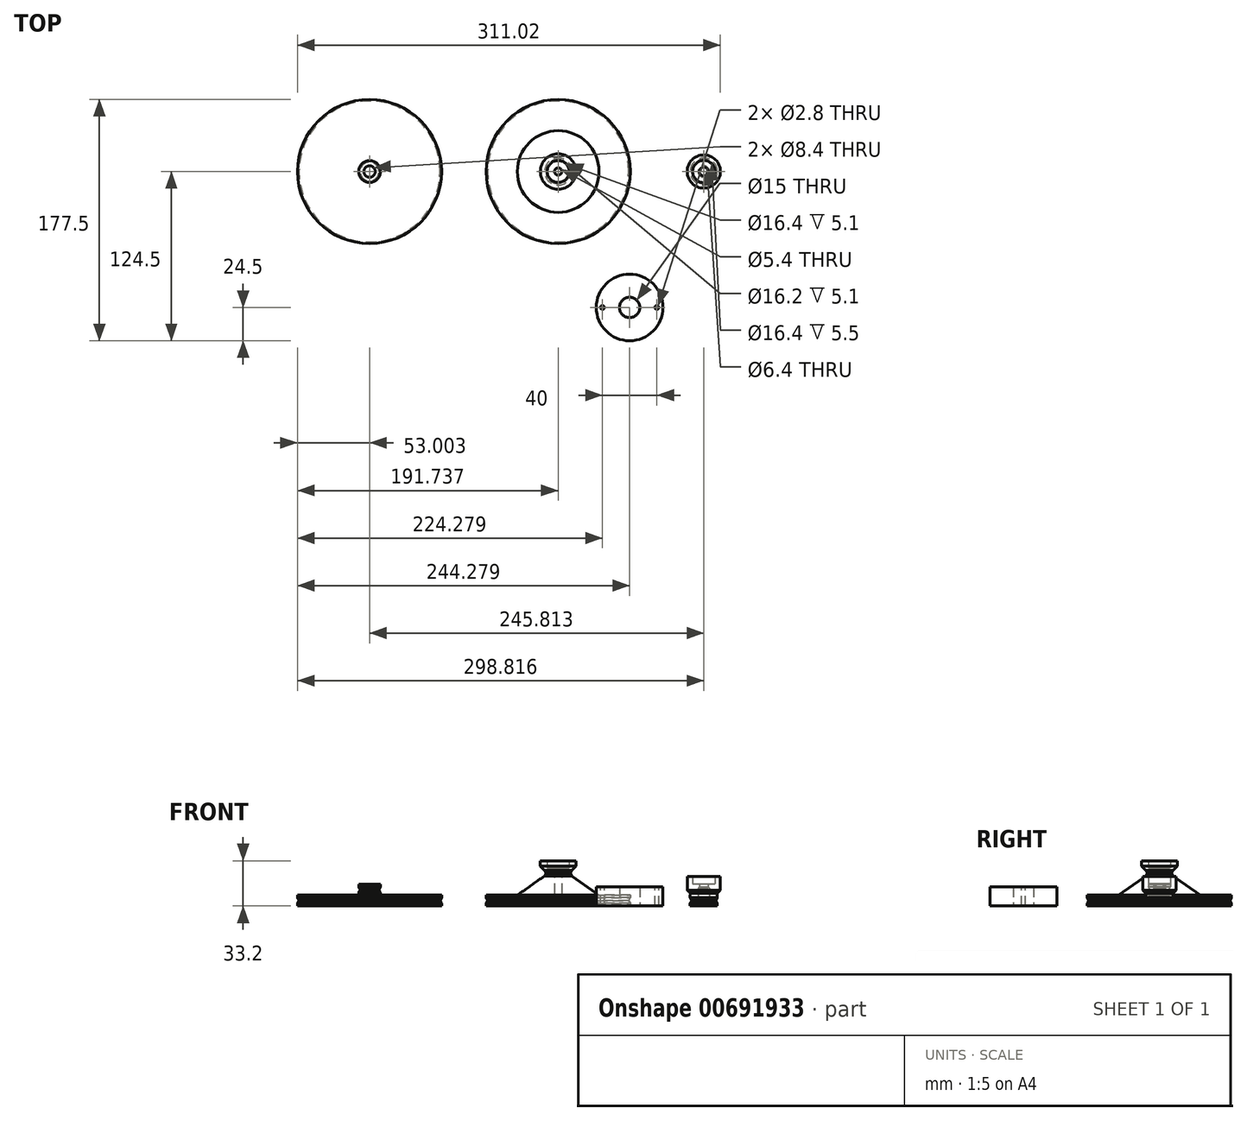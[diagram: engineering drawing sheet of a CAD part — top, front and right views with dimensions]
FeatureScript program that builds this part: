
annotation { "Feature Type Name" : "Feature", "Feature Type Description" : "" }
export const myFeature = defineFeature(function(context is Context, id is Id, definition is map)
    precondition{}
    {
        {
            var Q0;
            Q0=qCreatedBy(makeId("Front.planeOp"),FACE);
            var sketch = newSketch(context, id + "F0", { "sketchPlane" : qUnion([Q0])});
            skLineSegment(sketch, "E0", {"start": v(-130.12, 0) * mm, "end": v(-130.12, 2) * mm});
            skLineSegment(sketch, "E1", {"start": v(-130.12, 8) * mm, "end": v(-87.12, 8) * mm});
            skLineSegment(sketch, "E2", {"start": v(-87.12, 8) * mm, "end": v(-87.12, 22.1) * mm});
            skLineSegment(sketch, "E3", {"start": v(-87.12, 28.1) * mm, "end": v(-79.82, 28.1) * mm});
            skLineSegment(sketch, "E4", {"start": v(-79.82, 28.1) * mm, "end": v(-79.82, 0) * mm});
            skLineSegment(sketch, "E5", {"start": v(-79.82, 0) * mm, "end": v(-130.12, 0) * mm});
            skLineSegment(sketch, "E6", {"start": v(-130.12, 6) * mm, "end": v(-128.97, 4) * mm});
            skLineSegment(sketch, "E7", {"start": v(-128.97, 4) * mm, "end": v(-130.12, 2) * mm});
            skLineSegment(sketch, "E8", {"start": v(-87.12, 26.1) * mm, "end": v(-85.97, 24.1) * mm});
            skLineSegment(sketch, "E9", {"start": v(-85.97, 24.1) * mm, "end": v(-87.12, 22.1) * mm});
            skLineSegment(sketch, "E10.trimOffspring", {"start": v(-87.12, 26.1) * mm, "end": v(-87.12, 28.1) * mm});
            skLineSegment(sketch, "E11.trimOffspring", {"start": v(-130.12, 6) * mm, "end": v(-130.12, 8) * mm});
            skLineSegment(sketch, "E12", {"start": v(-77.12, 0) * mm, "end": v(-77.12, 16.17) * mm, "construction": true});
            skLineSegment(sketch, "E13", {"start": v(25.76, 0) * mm, "end": v(25.76, 16.21) * mm});
            skLineSegment(sketch, "E14", {"start": v(25.76, 16.21) * mm, "end": v(21.76, 16.21) * mm});
            skLineSegment(sketch, "E15", {"start": v(21.76, 16.21) * mm, "end": v(21.76, 21.71) * mm});
            skLineSegment(sketch, "E16", {"start": v(21.76, 21.71) * mm, "end": v(17.76, 21.71) * mm});
            skLineSegment(sketch, "E17", {"start": v(17.76, 21.71) * mm, "end": v(17.76, 11.68) * mm});
            skLineSegment(sketch, "E18", {"start": v(29.96, 0) * mm, "end": v(29.96, 12.69) * mm, "construction": true});
            skLineSegment(sketch, "E19", {"start": v(19.96, 0) * mm, "end": v(19.96, 2) * mm});
            skLineSegment(sketch, "E20", {"start": v(19.96, 2) * mm, "end": v(21.11, 4) * mm});
            skLineSegment(sketch, "E21", {"start": v(21.11, 4) * mm, "end": v(19.96, 6) * mm});
            skLineSegment(sketch, "E22", {"start": v(17.76, 11.68) * mm, "end": v(19.98, 9.41) * mm});
            skLineSegment(sketch, "E23", {"start": v(25.76, 0) * mm, "end": v(19.96, 0) * mm});
            skLineSegment(sketch, "E24", {"start": v(19.98, 9.41) * mm, "end": v(19.96, 6) * mm});
            skLineSegment(sketch, "E25", {"start": v(25.76, 16.21) * mm, "end": v(26.76, 16.21) * mm});
            skLineSegment(sketch, "E26", {"start": v(26.76, 16.21) * mm, "end": v(26.76, 14.02) * mm});
            skLineSegment(sketch, "E27", {"start": v(26.76, 14.02) * mm, "end": v(25.76, 13.02) * mm});
            skLineSegment(sketch, "E28", {"start": v(-268.86, 0) * mm, "end": v(-268.86, 2) * mm});
            skLineSegment(sketch, "E29", {"start": v(-268.86, 8) * mm, "end": v(-223.86, 8) * mm});
            skLineSegment(sketch, "E30", {"start": v(-223.86, 8) * mm, "end": v(-223.86, 10) * mm});
            skLineSegment(sketch, "E31", {"start": v(-223.86, 16) * mm, "end": v(-220.06, 16) * mm});
            skLineSegment(sketch, "E32", {"start": v(-220.06, 16) * mm, "end": v(-220.06, 0) * mm});
            skLineSegment(sketch, "E33", {"start": v(-220.06, 0) * mm, "end": v(-268.86, 0) * mm});
            skLineSegment(sketch, "E34", {"start": v(-268.86, 6) * mm, "end": v(-267.7, 4) * mm});
            skLineSegment(sketch, "E35", {"start": v(-267.7, 4) * mm, "end": v(-268.86, 2) * mm});
            skLineSegment(sketch, "E36", {"start": v(-223.86, 14) * mm, "end": v(-222.7, 12) * mm});
            skLineSegment(sketch, "E37", {"start": v(-222.7, 12) * mm, "end": v(-223.86, 10) * mm});
            skLineSegment(sketch, "E38.trimOffspring", {"start": v(-223.86, 14) * mm, "end": v(-223.86, 16) * mm});
            skLineSegment(sketch, "E39.trimOffspring", {"start": v(-268.86, 6) * mm, "end": v(-268.86, 8) * mm});
            skLineSegment(sketch, "E40", {"start": v(-215.86, 0) * mm, "end": v(-215.86, 22.9) * mm, "construction": true});
            skLineSegment(sketch, "E41", {"start": v(-224.06, 0) * mm, "end": v(-224.06, -5.1) * mm});
            skLineSegment(sketch, "E42", {"start": v(-224.06, -5.1) * mm, "end": v(-234.06, -5.1) * mm});
            skLineSegment(sketch, "E43", {"start": v(-234.06, -5.1) * mm, "end": v(-234.06, 0) * mm});
            skLineSegment(sketch, "E44", {"start": v(-79.82, 5.1) * mm, "end": v(-85.32, 5.1) * mm});
            skLineSegment(sketch, "E45", {"start": v(-85.32, 5.1) * mm, "end": v(-85.32, 0) * mm});
            skLineSegment(sketch, "E46", {"start": v(-87.12, 22.1) * mm, "end": v(-107.16, 8) * mm});
            skLineSegment(sketch, "E47", {"start": v(-85.22, 28.1) * mm, "end": v(-85.22, 33.2) * mm});
            skLineSegment(sketch, "E48", {"start": v(-85.22, 33.2) * mm, "end": v(-90.22, 33.2) * mm});
            skLineSegment(sketch, "E49", {"start": v(-90.22, 33.2) * mm, "end": v(-90.22, 29.2) * mm});
            skLineSegment(sketch, "E50", {"start": v(-90.22, 29.2) * mm, "end": v(-87.12, 26.1) * mm});
            skSolve(sketch);
        }
        {
            var Q0;
            {var subQ0=sQuery(id+"F0.wireOp",EDGE,"E25");Q0=makeQuery(id+"F0.imprint","IMPRINT",FACE,{"disambiguationData":[TD([[makeQuery(id+"F0.imprint","IMPRINT",EDGE,{"derivedFrom":subQ0}),-1.0]])]});}
            var Q1;
            {var subQ3=sQuery(id+"F0.wireOp",EDGE,"E14");Q1=makeQuery(id+"F0.imprint","IMPRINT",FACE,{"disambiguationData":[TD([[makeQuery(id+"F0.imprint","IMPRINT",EDGE,{"derivedFrom":subQ3}),1.0]])]});}
            var Q2;
            Q2=sQuery(id+"F0.wireOp",EDGE,"E18");
            revolve(context, id + "F1", {"surfaceOperationType" : NewSurfaceOperationType.NEW, "entities" : qUnion([Q0, Q1]), "axis" : qUnion([Q2]), "revolveType" : RevolveType.FULL});
        }
        {
            var Q0;
            Q0=makeQuery(id+"F0.imprint","IMPRINT",FACE,{"disambiguationData":[TD([[makeQuery(id+"F0.imprint","IMPRINT",EDGE,{"derivedFrom":sQuery(id+"F0.wireOp",EDGE,"E0")}),-1.0]])]});
            var Q1;
            {var subQ1=sQuery(id+"F0.wireOp",EDGE,"E10.trimOffspring");Q1=makeQuery(id+"F0.imprint","IMPRINT",FACE,{"disambiguationData":[TD([[makeQuery(id+"F0.imprint","IMPRINT",EDGE,{"derivedFrom":subQ1}),1.0]])]});}
            var Q2;
            {var subQ0=sQuery(id+"F0.wireOp",EDGE,"E2");Q2=makeQuery(id+"F0.imprint","IMPRINT",FACE,{"disambiguationData":[TD([[makeQuery(id+"F0.imprint","IMPRINT",EDGE,{"derivedFrom":subQ0}),1.0]])]});}
            var Q3;
            Q3=sQuery(id+"F0.wireOp",EDGE,"E12");
            revolve(context, id + "F2", {"surfaceOperationType" : NewSurfaceOperationType.NEW, "entities" : qUnion([Q0, Q1, Q2]), "axis" : qUnion([Q3]), "revolveType" : RevolveType.FULL});
        }
        {
            var Q0;
            Q0=makeQuery(id+"F0.imprint","IMPRINT",FACE,{"disambiguationData":[TD([[makeQuery(id+"F0.imprint","IMPRINT",EDGE,{"derivedFrom":sQuery(id+"F0.wireOp",EDGE,"E28")}),-1.0]])]});
            var Q1;
            Q1=sQuery(id+"F0.wireOp",EDGE,"E40");
            revolve(context, id + "F3", {"surfaceOperationType" : NewSurfaceOperationType.NEW, "entities" : qUnion([Q0]), "axis" : qUnion([Q1]), "revolveType" : RevolveType.FULL});
        }
        {
            var Q0;
            Q0=qCreatedBy(makeId("Front.planeOp"),FACE);
            cPlane(context, id + "F4", {"entities" : qUnion([Q0]), "cplaneType" : CPlaneType.OFFSET, "offset" : 100 * mm, "width" : 150 * mm, "height" : 150 * mm});
        }
        {
            var Q0;
            Q0=qCreatedBy(id+"F4.planeOp",FACE);
            var sketch = newSketch(context, id + "F5", { "sketchPlane" : qUnion([Q0])});
            skLineSegment(sketch, "E51", {"start": v(-49.08, 0) * mm, "end": v(-49.08, 14.1) * mm});
            skLineSegment(sketch, "E52", {"start": v(-32.08, 0) * mm, "end": v(-49.08, 0) * mm});
            skLineSegment(sketch, "E53", {"start": v(-24.58, 0) * mm, "end": v(-24.58, 15.37) * mm, "construction": true});
            skLineSegment(sketch, "E54", {"start": v(-32.08, 0) * mm, "end": v(-32.08, 14.1) * mm});
            skLineSegment(sketch, "E55", {"start": v(-32.08, 14.1) * mm, "end": v(-49.08, 14.1) * mm});
            skSolve(sketch);
        }
        {
            var Q0;
            Q0=makeQuery(id+"F5.imprint","IMPRINT",FACE,{"disambiguationData":[TD([[makeQuery(id+"F5.imprint","IMPRINT",EDGE,{"derivedFrom":sQuery(id+"F5.wireOp",EDGE,"E51")}),-1.0]])]});
            var Q1;
            Q1=sQuery(id+"F5.wireOp",EDGE,"E53");
            revolve(context, id + "F6", {"surfaceOperationType" : NewSurfaceOperationType.NEW, "entities" : qUnion([Q0]), "axis" : qUnion([Q1]), "revolveType" : RevolveType.FULL});
        }
        {
            var Q0;
            Q0=makeQuery(id+"F6.opRevolve","SWEPT_FACE",FACE,{"disambiguationData":[OSD([sQuery(id+"F5.wireOp",EDGE,"E55")])]});
            var sketch = newSketch(context, id + "F7", { "sketchPlane" : qUnion([Q0])});
            skCircle(sketch, "E56", {"center": v(-44.58, -100) * mm, "radius": 1.4 * mm});
            skPoint(sketch, "E57", {"position": v(-24.58, -100) * mm});
            skLineSegment(sketch, "E58", {"start": v(-24.58, -100) * mm, "end": v(-24.58, -86.64) * mm, "construction": true});
            skCircle(sketch, "E59.MirrorC", {"center": v(-4.58, -100) * mm, "radius": 1.4 * mm});
            skSolve(sketch);
        }
        {
            var Q0;
            Q0 = qSketchRegion(id + "F7", true);
            extrude(context, id + "F8", {"entities" : qUnion([Q0]), "operationType" : NewBodyOperationType.REMOVE, "oppositeDirection" : true, "depth" : 25 * mm, "offsetDistance" : 25 * mm});
        }
    });
